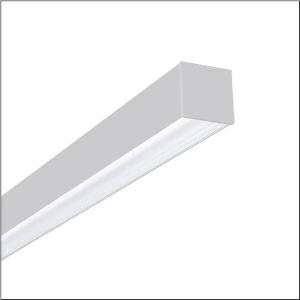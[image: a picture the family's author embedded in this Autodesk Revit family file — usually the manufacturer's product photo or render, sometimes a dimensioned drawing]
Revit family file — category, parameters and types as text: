
# Revit family: silica_r_5mx21bd1w4a_a515
name_source: partatom
category: Lighting Fixtures
units: mm (PartAtom-declared; Revit-internal decimal feet)

## family parameters
Cut with Voids When Loaded = No
Host = Face
Light Source = No
Part Type = Normal
Room Calculation Point = No
Round Connector Dimension = Use Diameter
Shared = No

## types (1)
- --- (1 x LED, 4950 lm, 29.3 W, 4000K)
    Apparent Load = 29 VA
    CIE Flux Codes = 82 97 100 100 100
    Color Rendering = 80
    Color Temperature = 4000K
    Default Elevation = 1800 mm
    Description = Silica®, office luminaire, of aluminium, light emission: direct distribution, primary light characteristic: symmetric, installation type: surface-mounted, LED, rated luminous flux: 4.950lm, luminous efficacy: 169lm/W, light colour: 840, colour temperature: 4000K, control gear: ECG DALI, with terminal, 3+2-pole, max. 2.5mm², mains connection: 230V, AC, 50/60Hz, rated input power: 29W, luminaire housing, of aluminium, traffic white (RAL 9016), length: 1.442mm, width: 65mm, height: 64mm, protection rating (complete): IP20, insulation class (complete): insulation class I (protective earthing), certification: CE, permissible operating ambient temperature: 0..+35°C, standard: EN 50419, packaging unit: 1 piece
    Height = 64 mm
    Lamp = 1 x LED
    Lamp Light Flux = 4950 lm
    Lamp Power = 29.3 W
    Lamp count = 1
    Length = 1442 mm
    Luminous efficacy = 169 lm/W
    Manufacturer = Siteco
    ModVariant = No
    Model = 5MX21BD1W4A
    Mounting Place = Ceiling
    Mounting Type = Surface mounted
    Number of Poles = 1
    OnlyDefault = Yes
    Power Factor = 1
    Product Name = Silica®
    Product group = office luminaire | ceiling mounted
    ProductGroupID = 300
    Protection Class = Protection class I
    Protection Degree = IP 20
    RLX_Detail_Level = 1
    RLX_Emergency_Light_Flux = 0 lm
    RLX_Emergency_Type = 0
    RLX_Emergency_Type_DB = No
    RlxData = <blob elided: 23381 chars, md5=92fba8c9>
    Socket = socket
    Standby Power = 0 W
    System Light Flux = 4950 lm
    System Power = 29 W
    Type Comments = factory setting: luminous flux: 100 % | dim-lin: 254 | 163 mA
    Type Image = l_1003937.jpg
    URL = http://relux.com
    VarID = @adj_155424
    Voltage = 0 V
    Weight = 0.00 kg
    Width = 66 mm

## geometry (parser evidence)
native form markers: Blend x4, Sweep x13
no freeform markers — native parametric forms only
